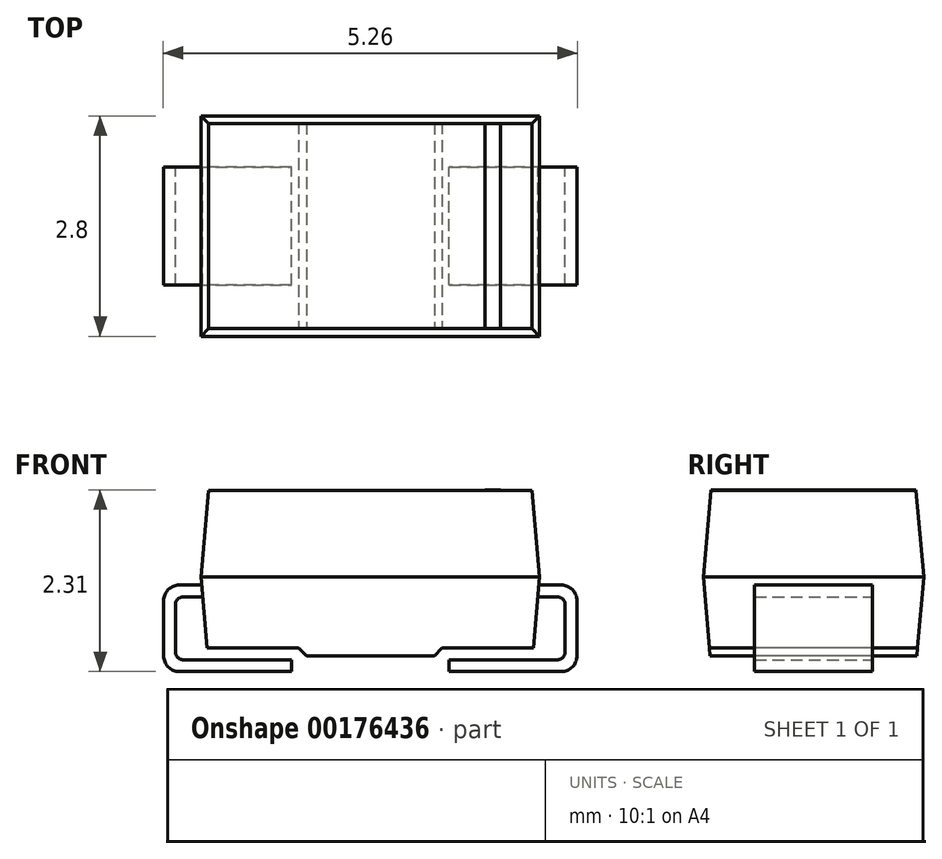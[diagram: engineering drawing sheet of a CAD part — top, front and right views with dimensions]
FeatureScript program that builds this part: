
annotation { "Feature Type Name" : "Feature", "Feature Type Description" : "" }
export const myFeature = defineFeature(function(context is Context, id is Id, definition is map)
    precondition{}
    {
        {
            var Q0;
            Q0=qCreatedBy(makeId("Top.planeOp"),FACE);
            var sketch = newSketch(context, id + "F0", { "sketchPlane" : qUnion([Q0])});
            skLineSegment(sketch, "E0.bottom", {"start": v(2.15, 1.4) * mm, "end": v(-2.15, 1.4) * mm});
            skLineSegment(sketch, "E0.top", {"start": v(2.15, -1.4) * mm, "end": v(-2.15, -1.4) * mm});
            skLineSegment(sketch, "E0.left", {"start": v(2.15, 1.4) * mm, "end": v(2.15, -1.4) * mm});
            skLineSegment(sketch, "E0.right", {"start": v(-2.15, 1.4) * mm, "end": v(-2.15, -1.4) * mm});
            skPoint(sketch, "E0.middle", {"position": v(0, 0) * mm});
            skSolve(sketch);
        }
        {
            var Q0;
            Q0=qSketchRegion(id+"F0",true);
            extrude(context, id + "F1", {"entities" : qUnion([Q0]), "depth" : 1.1 * mm, "hasDraft" : true, "draftAngle" : 5 * degree, "draftPullDirection" : true});
        }
        {
            var Q0;
            Q0=qSketchRegion(id+"F0",true);
            extrude(context, id + "F2", {"entities" : qUnion([Q0]), "operationType" : NewBodyOperationType.ADD, "oppositeDirection" : true, "depth" : 1 * mm, "hasDraft" : true, "draftAngle" : 5 * degree, "draftPullDirection" : true});
        }
        {
            var Q0;
            Q0=qCreatedBy(makeId("Front.planeOp"),FACE);
            var sketch = newSketch(context, id + "F3", { "sketchPlane" : qUnion([Q0])});
            skLineSegment(sketch, "E1", {"start": v(-2.14, -0.1) * mm, "end": v(-2.62, -0.1) * mm});
            skLineSegment(sketch, "E2", {"start": v(-2.62, -0.1) * mm, "end": v(-2.62, -1.2) * mm});
            skLineSegment(sketch, "E3", {"start": v(-2.62, -1.2) * mm, "end": v(-1, -1.2) * mm});
            skLineSegment(sketch, "E4", {"start": v(-1, -1.2) * mm, "end": v(-1, -1.05) * mm});
            skLineSegment(sketch, "E5", {"start": v(-1, -1.05) * mm, "end": v(-2.47, -1.05) * mm});
            skLineSegment(sketch, "E6", {"start": v(-2.47, -1.05) * mm, "end": v(-2.47, -0.25) * mm});
            skLineSegment(sketch, "E7", {"start": v(-2.47, -0.25) * mm, "end": v(-2.13, -0.25) * mm});
            skLineSegment(sketch, "E8", {"start": v(-2.13, -0.25) * mm, "end": v(-2.14, -0.1) * mm});
            skLineSegment(sketch, "E9", {"start": v(-2.47, -0.25) * mm, "end": v(-2.47, -0.1) * mm, "construction": true});
            skLineSegment(sketch, "E10", {"start": v(-2.47, -0.25) * mm, "end": v(-2.62, -0.25) * mm, "construction": true});
            skLineSegment(sketch, "E11", {"start": v(0, 0) * mm, "end": v(0, 1.1) * mm, "construction": true});
            skLineSegment(sketch, "E12.MirrorCS", {"start": v(2.13, -0.25) * mm, "end": v(2.14, -0.1) * mm});
            skLineSegment(sketch, "E13.MirrorCS", {"start": v(1, -1.2) * mm, "end": v(1, -1.05) * mm});
            skLineSegment(sketch, "E14.MirrorCS", {"start": v(2.47, -0.25) * mm, "end": v(2.47, -0.1) * mm, "construction": true});
            skLineSegment(sketch, "E15.MirrorCS", {"start": v(2.47, -0.25) * mm, "end": v(2.62, -0.25) * mm, "construction": true});
            skLineSegment(sketch, "E16.MirrorCS", {"start": v(2.47, -0.25) * mm, "end": v(2.13, -0.25) * mm});
            skLineSegment(sketch, "E17.MirrorCS", {"start": v(2.47, -1.05) * mm, "end": v(2.47, -0.25) * mm});
            skLineSegment(sketch, "E18.MirrorCS", {"start": v(1, -1.05) * mm, "end": v(2.47, -1.05) * mm});
            skLineSegment(sketch, "E19.MirrorCS", {"start": v(2.14, -0.1) * mm, "end": v(2.62, -0.1) * mm});
            skLineSegment(sketch, "E20.MirrorCS", {"start": v(2.62, -1.2) * mm, "end": v(1, -1.2) * mm});
            skLineSegment(sketch, "E21.MirrorCS", {"start": v(2.62, -0.1) * mm, "end": v(2.62, -1.2) * mm});
            skSolve(sketch);
        }
        {
            var Q0;
            Q0=qSketchRegion(id+"F3",true);
            extrude(context, id + "F4", {"entities" : qUnion([Q0]), "endBound" : BoundingType.SYMMETRIC, "depth" : 1.5 * mm});
        }
        {
            var Q0;
            Q0=makeQuery(id+"F4.opExtrude","SWEPT_EDGE",EDGE,{"disambiguationData":[OSD([sQuery(id+"F3.wireOp",EDGE,"E1"),sQuery(id+"F3.wireOp",EDGE,"E2")])]});
            var Q1;
            Q1=makeQuery(id+"F4.opExtrude","SWEPT_EDGE",EDGE,{"disambiguationData":[OSD([sQuery(id+"F3.wireOp",EDGE,"E19.MirrorCS"),sQuery(id+"F3.wireOp",EDGE,"E21.MirrorCS")])]});
            var Q2;
            Q2=makeQuery(id+"F4.opExtrude","SWEPT_EDGE",EDGE,{"disambiguationData":[OSD([sQuery(id+"F3.wireOp",EDGE,"E2"),sQuery(id+"F3.wireOp",EDGE,"E3")])]});
            var Q3;
            Q3=makeQuery(id+"F4.opExtrude","SWEPT_EDGE",EDGE,{"disambiguationData":[OSD([sQuery(id+"F3.wireOp",EDGE,"E20.MirrorCS"),sQuery(id+"F3.wireOp",EDGE,"E21.MirrorCS")])]});
            fillet(context, id + "F5", {"entities" : qUnion([Q0, Q1, Q2, Q3]), "radius" : 0.2 * mm, "tangentPropagation" : true, "allowEdgeOverflow" : false});
        }
        {
            var Q0;
            Q0=makeQuery(id+"F4.opExtrude","SWEPT_EDGE",EDGE,{"disambiguationData":[OSD([sQuery(id+"F3.wireOp",EDGE,"E6"),sQuery(id+"F3.wireOp",EDGE,"E7")])]});
            var Q1;
            Q1=makeQuery(id+"F4.opExtrude","SWEPT_EDGE",EDGE,{"disambiguationData":[OSD([sQuery(id+"F3.wireOp",EDGE,"E17.MirrorCS"),sQuery(id+"F3.wireOp",EDGE,"E18.MirrorCS")])]});
            var Q2;
            Q2=makeQuery(id+"F4.opExtrude","SWEPT_EDGE",EDGE,{"disambiguationData":[OSD([sQuery(id+"F3.wireOp",EDGE,"E5"),sQuery(id+"F3.wireOp",EDGE,"E6")])]});
            var Q3;
            Q3=makeQuery(id+"F4.opExtrude","SWEPT_EDGE",EDGE,{"disambiguationData":[OSD([sQuery(id+"F3.wireOp",EDGE,"E16.MirrorCS"),sQuery(id+"F3.wireOp",EDGE,"E17.MirrorCS")])]});
            fillet(context, id + "F6", {"entities" : qUnion([Q0, Q1, Q2, Q3]), "radius" : 0.1 * mm, "tangentPropagation" : true, "allowEdgeOverflow" : false});
        }
        {
            var Q0;
            Q0=qCreatedBy(makeId("Front.planeOp"),FACE);
            var sketch = newSketch(context, id + "F7", { "sketchPlane" : qUnion([Q0])});
            skLineSegment(sketch, "E22", {"start": v(2.07, -0.9) * mm, "end": v(0.91, -0.9) * mm});
            skLineSegment(sketch, "E23", {"start": v(0.91, -0.9) * mm, "end": v(0.81, -1) * mm});
            skLineSegment(sketch, "E24", {"start": v(0.81, -1) * mm, "end": v(2.06, -1) * mm});
            skLineSegment(sketch, "E25", {"start": v(2.06, -1) * mm, "end": v(2.07, -0.9) * mm});
            skLineSegment(sketch, "E26", {"start": v(0, 0) * mm, "end": v(0, -1.2) * mm, "construction": true});
            skLineSegment(sketch, "E27.MirrorCS", {"start": v(-2.06, -1) * mm, "end": v(-2.07, -0.9) * mm});
            skLineSegment(sketch, "E28.MirrorCS", {"start": v(-0.81, -1) * mm, "end": v(-2.06, -1) * mm});
            skLineSegment(sketch, "E29.MirrorCS", {"start": v(-0.91, -0.9) * mm, "end": v(-0.81, -1) * mm});
            skLineSegment(sketch, "E30.MirrorCS", {"start": v(-2.07, -0.9) * mm, "end": v(-0.91, -0.9) * mm});
            skSolve(sketch);
        }
        {
            var Q0;
            Q0=qSketchRegion(id+"F7",true);
            extrude(context, id + "F8", {"entities" : qUnion([Q0]), "operationType" : NewBodyOperationType.REMOVE, "endBound" : BoundingType.SYMMETRIC, "oppositeDirection" : true, "depth" : 25 * mm});
        }
        {
            var Q0;
            Q0=makeQuery(id+"F1.opExtrude","CAP_FACE",FACE,{"disambiguationData":[OSD([sQuery(id+"F0.wireOp",EDGE,"E0.bottom"),sQuery(id+"F0.wireOp",EDGE,"E0.top"),sQuery(id+"F0.wireOp",EDGE,"E0.left"),sQuery(id+"F0.wireOp",EDGE,"E0.right")])],"isStart":false});
            var sketch = newSketch(context, id + "F9", { "sketchPlane" : qUnion([Q0])});
            skLineSegment(sketch, "E31.bottom", {"start": v(1.65, -1.3) * mm, "end": v(1.45, -1.3) * mm});
            skLineSegment(sketch, "E31.top", {"start": v(1.65, 1.3) * mm, "end": v(1.45, 1.3) * mm});
            skLineSegment(sketch, "E31.left", {"start": v(1.65, -1.3) * mm, "end": v(1.65, 1.3) * mm});
            skLineSegment(sketch, "E31.right", {"start": v(1.45, -1.3) * mm, "end": v(1.45, 1.3) * mm});
            skSolve(sketch);
        }
        {
            var Q0;
            Q0=qSketchRegion(id+"F9",true);
            extrude(context, id + "F10", {"entities" : qUnion([Q0]), "depth" : 0.01 * mm});
        }
    });
